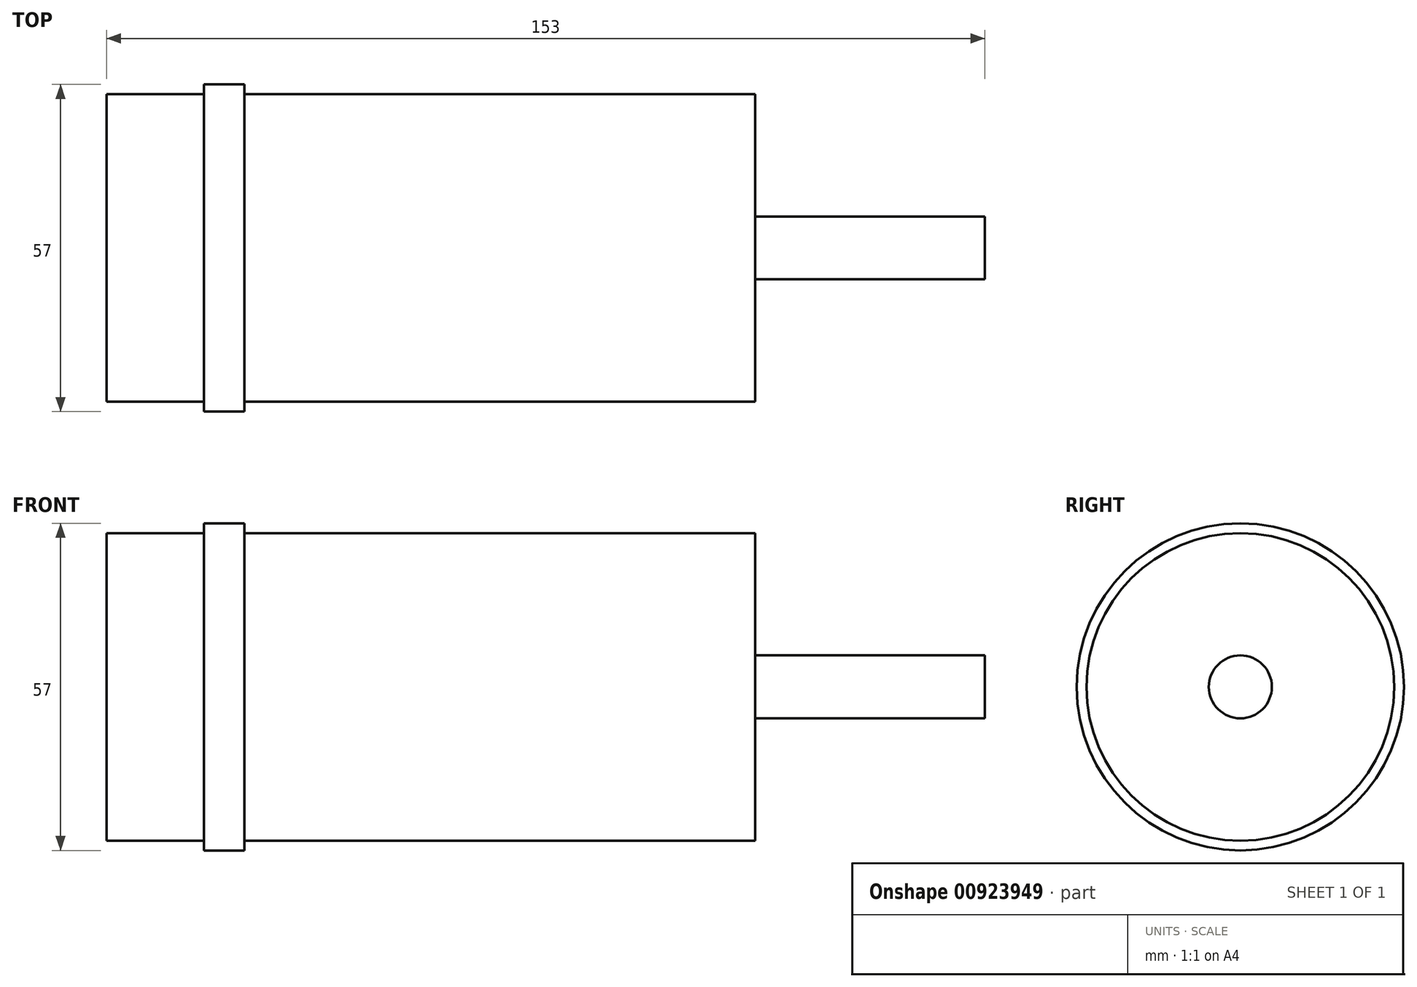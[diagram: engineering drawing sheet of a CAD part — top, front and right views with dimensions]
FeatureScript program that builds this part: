
annotation { "Feature Type Name" : "Feature", "Feature Type Description" : "" }
export const myFeature = defineFeature(function(context is Context, id is Id, definition is map)
    precondition{}
    {
        {
            var Q0;
            Q0=qCreatedBy(makeId("Front.planeOp"),FACE);
            var sketch = newSketch(context, id + "F0", { "sketchPlane" : qUnion([Q0])});
            skLineSegment(sketch, "E0", {"start": v(-76.37, 0) * mm, "end": v(94.17, 0) * mm, "construction": true});
            skLineSegment(sketch, "E1", {"start": v(-63.62, 0) * mm, "end": v(-63.62, 26.8) * mm});
            skLineSegment(sketch, "E2", {"start": v(-63.62, 26.8) * mm, "end": v(-46.62, 26.8) * mm});
            skLineSegment(sketch, "E3", {"start": v(-46.62, 26.8) * mm, "end": v(-46.62, 28.5) * mm});
            skLineSegment(sketch, "E4", {"start": v(-46.62, 28.5) * mm, "end": v(-39.62, 28.5) * mm});
            skLineSegment(sketch, "E5", {"start": v(-39.62, 28.5) * mm, "end": v(-39.62, 26.8) * mm});
            skLineSegment(sketch, "E6", {"start": v(-39.62, 26.8) * mm, "end": v(49.38, 26.8) * mm});
            skLineSegment(sketch, "E7", {"start": v(49.38, 26.8) * mm, "end": v(49.38, 5.49) * mm});
            skLineSegment(sketch, "E8", {"start": v(49.38, 5.49) * mm, "end": v(89.38, 5.49) * mm});
            skLineSegment(sketch, "E9", {"start": v(89.38, 5.49) * mm, "end": v(89.38, 0) * mm});
            skLineSegment(sketch, "E10", {"start": v(-63.62, 0) * mm, "end": v(89.38, 0) * mm});
            skSolve(sketch);
        }
        {
            var Q0;
            Q0 = qSketchRegion(id + "F0", true);
            var Q1;
            Q1=sQuery(id+"F0.wireOp",EDGE,"E10");
            revolve(context, id + "F1", {"surfaceOperationType" : NewSurfaceOperationType.NEW, "entities" : qUnion([Q0]), "axis" : qUnion([Q1]), "revolveType" : RevolveType.FULL});
        }
    });
